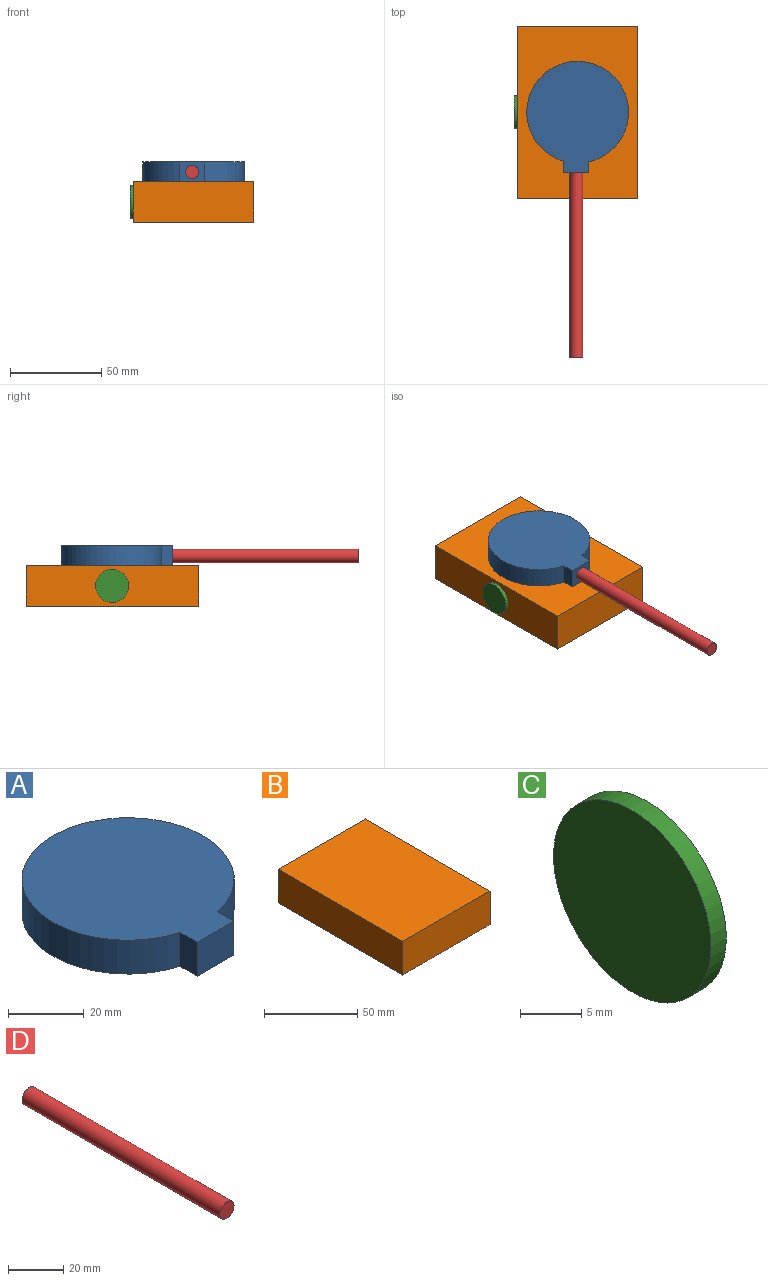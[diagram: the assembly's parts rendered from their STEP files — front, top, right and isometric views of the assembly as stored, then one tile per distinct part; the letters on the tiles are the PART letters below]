
ASSEMBLY  parts=4 mates=3
PART A: 6 faces, bbox 55.9x61.2x10.9 mm
  f0: cylinder r=27.93mm len=55.87mm, axis (0,0,-1), area 1766.4mm2, adj f1,f3,f4,f5
  f1: plane 10.92x6.39mm, normal (-1,0,0), area 69.8mm2, adj f0,f2,f4,f5
  f2: plane 13.65x10.92mm, normal (0,-1,0), area 149.1mm2, adj f1,f3,f4,f5
  f3: plane 10.92x6.02mm, normal (1,0,0), area 65.7mm2, adj f0,f2,f4,f5
  f4: plane 61.22x55.87mm, normal (0,0,1), area 2528.5mm2, adj f0,f1,f2,f3
  f5: plane 61.22x55.87mm, normal (0,0,-1), area 2528.5mm2, adj f0,f1,f2,f3
PART B: 6 faces, bbox 66x94.7x22.1 mm
  f0: plane 94.73x22.1mm, normal (-1,0,0), area 2093.4mm2, adj f1,f3,f4,f5
  f1: plane 66.03x22.1mm, normal (0,-1,0), area 1459.1mm2, adj f0,f2,f4,f5
  f2: plane 94.73x22.1mm, normal (1,0,0), area 2093.4mm2, adj f1,f3,f4,f5
  f3: plane 66.03x22.1mm, normal (0,1,0), area 1459.1mm2, adj f0,f2,f4,f5
  f4: plane 94.73x66.03mm, normal (0,0,1), area 6255.3mm2, adj f0,f1,f2,f3
  f5: plane 94.73x66.03mm, normal (0,0,-1), area 6255.3mm2, adj f0,f1,f2,f3
PART C: 3 faces, bbox 1.8x18.2x18.2 mm
  f0: cylinder r=9.11mm len=18.22mm, axis (1,0,0), area 101.8mm2, adj f1,f2
  f1: plane 18.22x18.22mm, normal (-1,0,0), area 260.8mm2, adj f0
  f2: plane 18.22x18.22mm, normal (1,0,0), area 260.8mm2, adj f0
PART D: 3 faces, bbox 7.3x101.6x7.3 mm
  f0: cylinder r=3.66mm len=101.6mm, axis (0,1,0), area 2338.6mm2, adj f1,f2
  f1: plane 7.33x7.33mm, normal (0,-1,0), area 42.2mm2, adj f0
  f2: plane 7.33x7.33mm, normal (0,1,0), area 42.2mm2, adj f0
PLACE A t=(-28.2,-17.74,-5.35)mm
PLACE B t=(-27.56,-10.69,-5.35)mm fixed
PLACE C t=(-27.56,21.25,-4.85)mm
PLACE D rot(axis=(0,1,0),180deg) t=(-29.69,-17.74,49.38)mm
MATE revolute A.f0 <-> B.f4  axis (0,0,-1) through (-28.2,-17.74,16.75)mm
MATE fastened D.f0 <-> A.f2  axis (0,1,0) through (-28.95,-51.03,22.21)mm
MATE revolute C.f0 <-> B.f0  axis (1,0,0) through (-61.22,-17.74,5.7)mm
